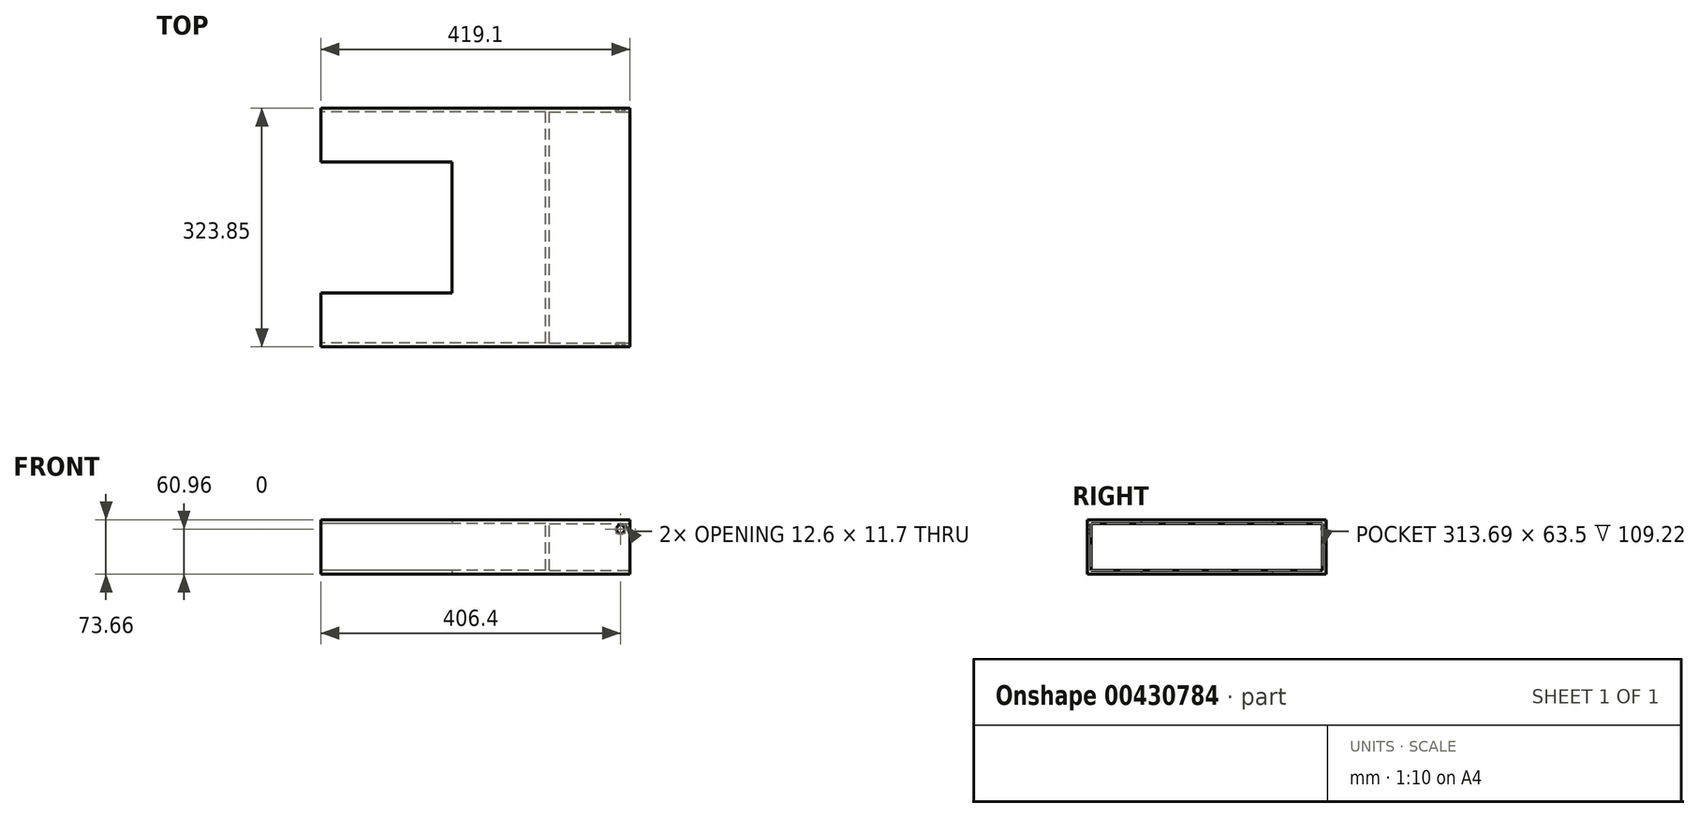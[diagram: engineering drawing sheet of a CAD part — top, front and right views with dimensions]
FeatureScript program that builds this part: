
annotation { "Feature Type Name" : "Feature", "Feature Type Description" : "" }
export const myFeature = defineFeature(function(context is Context, id is Id, definition is map)
    precondition{}
    {
        {
            var Q0;
            Q0=qCreatedBy(makeId("Front.planeOp"),FACE);
            var sketch = newSketch(context, id + "F0", { "sketchPlane" : qUnion([Q0])});
            skLineSegment(sketch, "E0.bottom", {"start": v(0, 0) * mm, "end": v(-419.1, 0) * mm});
            skLineSegment(sketch, "E0.top", {"start": v(0, 73.66) * mm, "end": v(-419.1, 73.66) * mm});
            skLineSegment(sketch, "E0.left", {"start": v(0, 0) * mm, "end": v(0, 73.66) * mm});
            skLineSegment(sketch, "E0.right", {"start": v(-419.1, 0) * mm, "end": v(-419.1, 73.66) * mm});
            skSolve(sketch);
        }
        {
            var Q0;
            Q0=makeQuery(id+"F0.imprint","IMPRINT",FACE,{"disambiguationData":[TD([[makeQuery(id+"F0.imprint","IMPRINT",EDGE,{"derivedFrom":sQuery(id+"F0.wireOp",EDGE,"E0.bottom")}),-1.0]])]});
            extrude(context, id + "F1", {"entities" : qUnion([Q0]), "depth" : 323.85 * mm, "offsetDistance" : 25.4 * mm});
        }
        {
            var Q0;
            Q0=makeQuery(id+"F1.opExtrude","SWEPT_FACE",FACE,{"disambiguationData":[OSD([sQuery(id+"F0.wireOp",EDGE,"E0.right")])]});
            var sketch = newSketch(context, id + "F2", { "sketchPlane" : qUnion([Q0])});
            skLineSegment(sketch, "E1.0", {"start": v(318.77, 68.58) * mm, "end": v(5.08, 68.58) * mm});
            skLineSegment(sketch, "E1.1", {"start": v(318.77, 5.08) * mm, "end": v(318.77, 68.58) * mm});
            skLineSegment(sketch, "E1.2", {"start": v(318.77, 5.08) * mm, "end": v(5.08, 5.08) * mm});
            skLineSegment(sketch, "E1.3", {"start": v(5.08, 5.08) * mm, "end": v(5.08, 68.58) * mm});
            skSolve(sketch);
        }
        {
            var Q0;
            Q0 = qSketchRegion(id + "F2", true);
            extrude(context, id + "F3", {"entities" : qUnion([Q0]), "operationType" : NewBodyOperationType.REMOVE, "oppositeDirection" : true, "depth" : 304.8 * mm, "offsetDistance" : 25.4 * mm});
        }
        {
            var Q0;
            Q0=makeQuery(id+"F1.opExtrude","SWEPT_FACE",FACE,{"disambiguationData":[OSD([sQuery(id+"F0.wireOp",EDGE,"E0.left")])]});
            var sketch = newSketch(context, id + "F4", { "sketchPlane" : qUnion([Q0])});
            skLineSegment(sketch, "E2.0", {"start": v(-5.08, 5.08) * mm, "end": v(-5.08, 68.58) * mm});
            skLineSegment(sketch, "E2.1", {"start": v(-318.77, 5.08) * mm, "end": v(-5.08, 5.08) * mm});
            skLineSegment(sketch, "E2.2", {"start": v(-318.77, 68.58) * mm, "end": v(-318.77, 5.08) * mm});
            skLineSegment(sketch, "E2.3", {"start": v(-5.08, 68.58) * mm, "end": v(-318.77, 68.58) * mm});
            skSolve(sketch);
        }
        {
            var Q0;
            Q0=makeQuery(id+"F4.imprint","IMPRINT",FACE,{"disambiguationData":[TD([[makeQuery(id+"F4.imprint","IMPRINT",EDGE,{"derivedFrom":sQuery(id+"F4.wireOp",EDGE,"E2.0")}),1.0]])]});
            extrude(context, id + "F5", {"entities" : qUnion([Q0]), "operationType" : NewBodyOperationType.REMOVE, "oppositeDirection" : true, "depth" : 109.22 * mm, "offsetDistance" : 25.4 * mm});
        }
        {
            var Q0;
            Q0=makeQuery(id+"F0.imprint","IMPRINT",FACE,{"disambiguationData":[TD([[makeQuery(id+"F0.imprint","IMPRINT",EDGE,{"derivedFrom":sQuery(id+"F0.wireOp",EDGE,"E0.bottom")}),-1.0]])]});
            var sketch = newSketch(context, id + "F6", { "sketchPlane" : qUnion([Q0])});
            skCircle(sketch, "E3.cCircle", {"center": v(-12.7, 60.96) * mm, "radius": 6.35 * mm, "construction": true});
            skLineSegment(sketch, "E3.0", {"start": v(-16.53, 55.9) * mm, "end": v(-19, 61.75) * mm});
            skLineSegment(sketch, "E3.1", {"start": v(-19, 61.75) * mm, "end": v(-15.17, 66.81) * mm});
            skLineSegment(sketch, "E3.2", {"start": v(-15.17, 66.81) * mm, "end": v(-8.87, 66.02) * mm});
            skLineSegment(sketch, "E3.3", {"start": v(-8.87, 66.02) * mm, "end": v(-6.4, 60.17) * mm});
            skLineSegment(sketch, "E3.4", {"start": v(-6.4, 60.17) * mm, "end": v(-10.23, 55.1) * mm});
            skLineSegment(sketch, "E3.5", {"start": v(-10.23, 55.1) * mm, "end": v(-16.53, 55.9) * mm});
            skSolve(sketch);
        }
        {
            var Q0;
            Q0 = qSketchRegion(id + "F6", true);
            var Q1;
            Q1=makeQuery(id+"F1.opExtrude","CAP_FACE",FACE,{"disambiguationData":[OSD([sQuery(id+"F0.wireOp",EDGE,"E0.bottom"),sQuery(id+"F0.wireOp",EDGE,"E0.top"),sQuery(id+"F0.wireOp",EDGE,"E0.left"),sQuery(id+"F0.wireOp",EDGE,"E0.right")])],"isStart":false});
            extrude(context, id + "F7", {"entities" : qUnion([Q0]), "operationType" : NewBodyOperationType.REMOVE, "endBound" : BoundingType.UP_TO_SURFACE, "depth" : 25.4 * mm, "endBoundEntityFace" : qUnion([Q1]), "offsetDistance" : 25.4 * mm});
        }
        {
            var Q0;
            Q0=makeQuery(id+"F1.opExtrude","SWEPT_FACE",FACE,{"disambiguationData":[OSD([sQuery(id+"F0.wireOp",EDGE,"E0.bottom")])]});
            var sketch = newSketch(context, id + "F8", { "sketchPlane" : qUnion([Q0])});
            skLineSegment(sketch, "E4.bottom", {"start": v(-419.1, 250.83) * mm, "end": v(-241.3, 250.83) * mm});
            skLineSegment(sketch, "E4.top", {"start": v(-419.1, 73.03) * mm, "end": v(-241.3, 73.03) * mm});
            skLineSegment(sketch, "E4.left", {"start": v(-419.1, 250.83) * mm, "end": v(-419.1, 73.03) * mm});
            skLineSegment(sketch, "E4.right", {"start": v(-241.3, 250.83) * mm, "end": v(-241.3, 73.03) * mm});
            skLineSegment(sketch, "E5", {"start": v(-419.1, 161.93) * mm, "end": v(0, 161.93) * mm, "construction": true});
            skSolve(sketch);
        }
        {
            var Q0;
            Q0 = qSketchRegion(id + "F8", true);
            extrude(context, id + "F9", {"entities" : qUnion([Q0]), "operationType" : NewBodyOperationType.REMOVE, "endBound" : BoundingType.THROUGH_ALL, "oppositeDirection" : true, "depth" : 25.4 * mm, "offsetDistance" : 25.4 * mm});
        }
    });
